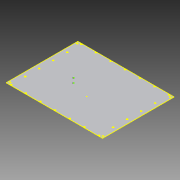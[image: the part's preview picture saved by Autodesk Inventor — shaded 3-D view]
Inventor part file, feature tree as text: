
AUTODESK INVENTOR PART (.ipt)
format: ipt  version: 2016 (Build 200138000, 138)  size: 175,104 bytes
history: native  units: in
note: dims shown in document units (in); Inventor stores cm internally (conversion verified against a paired STEP export)
features: hole x5, pattern_linear x5, sketch x4, extrude x1
ambient origin geometry x8: Origin, YZ Plane, XZ Plane, XY Plane, X Axis, Y Axis, Z Axis, Center Point
bodies: Solid1 (feature_tree)
feature tree (15):
  extrude  "Extrusion1"  Depth=10.75in
  sketch  "Sketch2"  dims[d3=0.06in d4=0.0in d7=0.0935in]
  hole  "Hole1"  [1 undecoded]
  pattern_linear  "Rectangular Pattern1"  Spacing1=0.25in  [1 undecoded]
  hole  "Hole2"  [1 undecoded]
  pattern_linear  "Rectangular Pattern2"  Count1=5 Spacing1=1.562in
  pattern_linear  "Rectangular Pattern3"  Count1=7 Spacing1=1.635in
  hole  "Hole3"  [1 undecoded]
  pattern_linear  "Rectangular Pattern4"  Spacing1=0.0935in  [1 undecoded]
  pattern_linear  "Rectangular Pattern5"  Count1=5 Spacing1=1.562in
  sketch  "Sketch3"  dims[d8=0.471in]
  sketch  "Sketch4"  dims[d9=0.1875in d10=0.25in d11=0.156in d12=0.75in d13=0.375in d14=0.25in d15=0.5635in d16=1.0in d17=0.8108in d18=0.7874in d20=10.375in d21=0.7874in d23=7.5in d24=0.096in d25=0.75in d26=0.16in d27=0.25in d28=0.5635in d29=1.0in d30=0.8108in d31=1.9685in d33=1.562in d34=2.7559in d36=1.635in d37=0.471in d38=0.0935in d39=0.096in d40=0.75in d41=0.16in d42=0.25in d43=0.5635in d44=1.0in d45=0.8108in d46=1.9685in d48=1.562in d49=2.7559in d51=1.635in d61=0.128in d62=0.75in d63=0.232in d64=0.25in d65=0.5635in d66=1.0in d67=0.8108in d68=0.128in d69=0.75in d70=0.232in d71=0.25in d72=0.5635in d73=1.0in d74=0.8108in]
  hole  "Hole5"  [1 undecoded]
  hole  "Hole6"  [1 undecoded]
  sketch  "Sketch1"  dims[d0=8.0in d2=10.75in]
note: 7 required parameter values undecoded (feature->parameter linkage not recoverable at this tier; creation-order binding heuristic only, values carry confidence <= 0.55)
